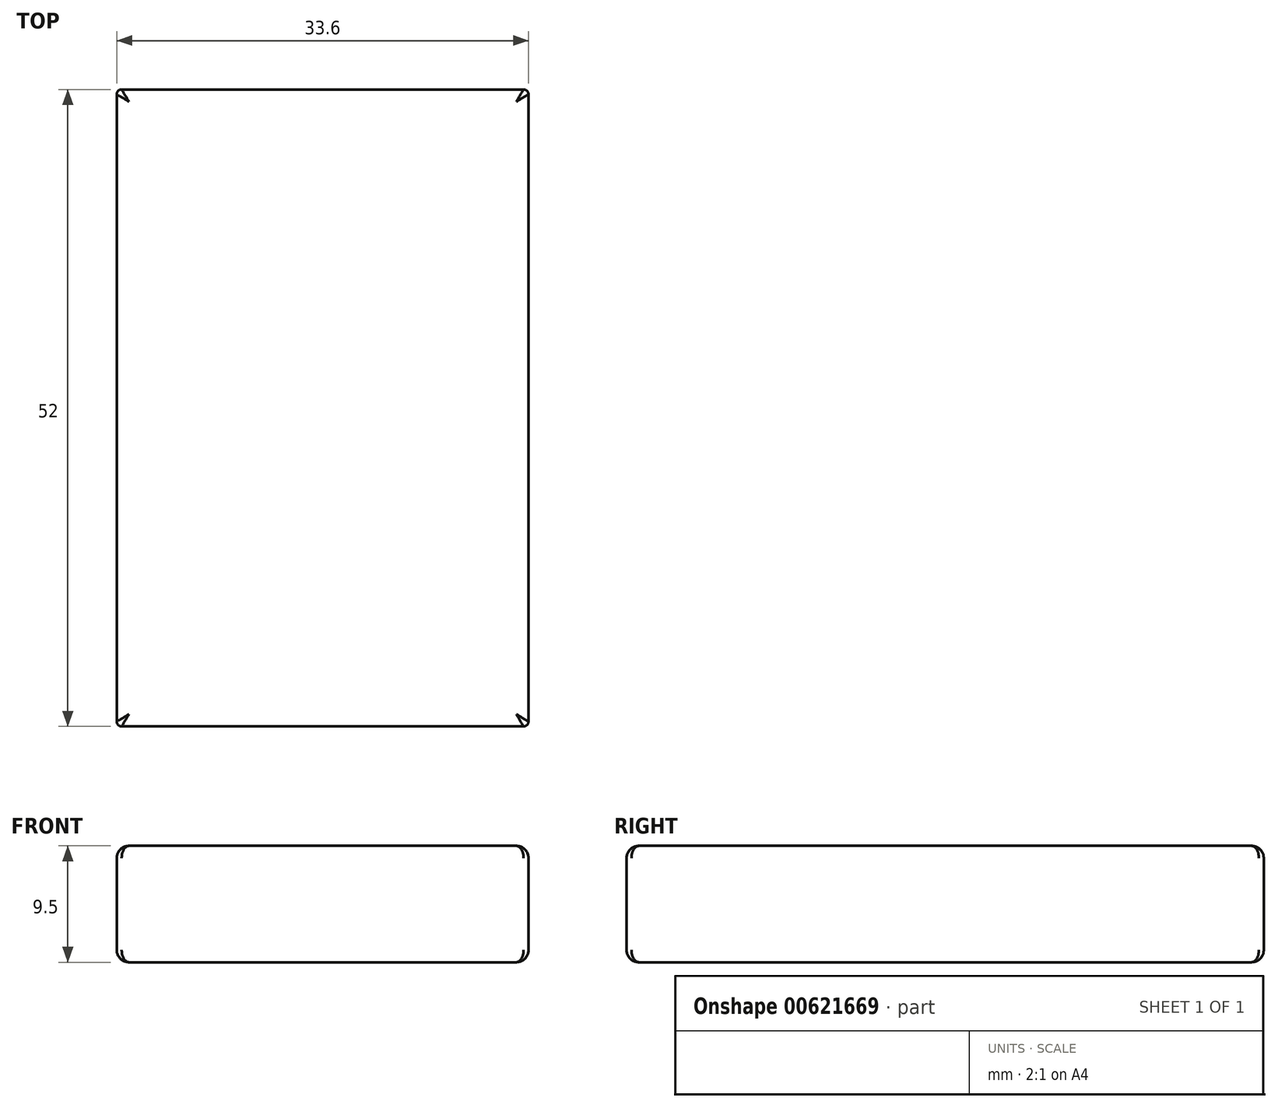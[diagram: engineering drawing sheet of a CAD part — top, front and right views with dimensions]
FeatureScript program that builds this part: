
annotation { "Feature Type Name" : "Feature", "Feature Type Description" : "" }
export const myFeature = defineFeature(function(context is Context, id is Id, definition is map)
    precondition{}
    {
        {
            var Q0;
            Q0=qCreatedBy(makeId("Top.planeOp"),FACE);
            var sketch = newSketch(context, id + "F0", { "sketchPlane" : qUnion([Q0])});
            skLineSegment(sketch, "E0.bottom", {"start": v(-16.8, 26) * mm, "end": v(16.8, 26) * mm});
            skLineSegment(sketch, "E0.top", {"start": v(-16.8, -26) * mm, "end": v(16.8, -26) * mm});
            skLineSegment(sketch, "E0.left", {"start": v(-16.8, 26) * mm, "end": v(-16.8, -26) * mm});
            skLineSegment(sketch, "E0.right", {"start": v(16.8, 26) * mm, "end": v(16.8, -26) * mm});
            skPoint(sketch, "E0.middle", {"position": v(0, 0) * mm});
            skSolve(sketch);
        }
        {
            var Q0;
            Q0=qSketchRegion(id+"F0",true);
            extrude(context, id + "F1", {"entities" : qUnion([Q0]), "depth" : 9.5 * mm, "offsetDistance" : 25 * mm});
        }
        {
            var Q0;
            Q0=makeQuery(id+"F1.opExtrude","SWEPT_EDGE",EDGE,{"disambiguationData":[OSD([sQuery(id+"F0.wireOp",EDGE,"E0.top"),sQuery(id+"F0.wireOp",EDGE,"E0.left")])]});
            var Q1;
            Q1=makeQuery(id+"F1.opExtrude","SWEPT_EDGE",EDGE,{"disambiguationData":[OSD([sQuery(id+"F0.wireOp",EDGE,"E0.top"),sQuery(id+"F0.wireOp",EDGE,"E0.right")])]});
            var Q2;
            Q2=makeQuery(id+"F1.opExtrude","SWEPT_EDGE",EDGE,{"disambiguationData":[OSD([sQuery(id+"F0.wireOp",EDGE,"E0.bottom"),sQuery(id+"F0.wireOp",EDGE,"E0.right")])]});
            var Q3;
            Q3=makeQuery(id+"F1.opExtrude","SWEPT_EDGE",EDGE,{"disambiguationData":[OSD([sQuery(id+"F0.wireOp",EDGE,"E0.bottom"),sQuery(id+"F0.wireOp",EDGE,"E0.left")])]});
            fillet(context, id + "F2", {"entities" : qUnion([Q0, Q1, Q2, Q3]), "radius" : .4 * mm, "tangentPropagation" : true, "allowEdgeOverflow" : false});
        }
        {
            var Q0;
            Q0=makeQuery(id+"F1.opExtrude","CAP_FACE",FACE,{"disambiguationData":[OSD([sQuery(id+"F0.wireOp",EDGE,"E0.bottom"),sQuery(id+"F0.wireOp",EDGE,"E0.top"),sQuery(id+"F0.wireOp",EDGE,"E0.left"),sQuery(id+"F0.wireOp",EDGE,"E0.right")])],"isStart":false});
            var Q1;
            Q1=makeQuery(id+"F1.opExtrude","CAP_FACE",FACE,{"disambiguationData":[OSD([sQuery(id+"F0.wireOp",EDGE,"E0.bottom"),sQuery(id+"F0.wireOp",EDGE,"E0.top"),sQuery(id+"F0.wireOp",EDGE,"E0.left"),sQuery(id+"F0.wireOp",EDGE,"E0.right")])],"isStart":true});
            fillet(context, id + "F3", {"entities" : qUnion([Q0, Q1]), "radius" : 1 * mm, "tangentPropagation" : true, "allowEdgeOverflow" : false});
        }
    });
